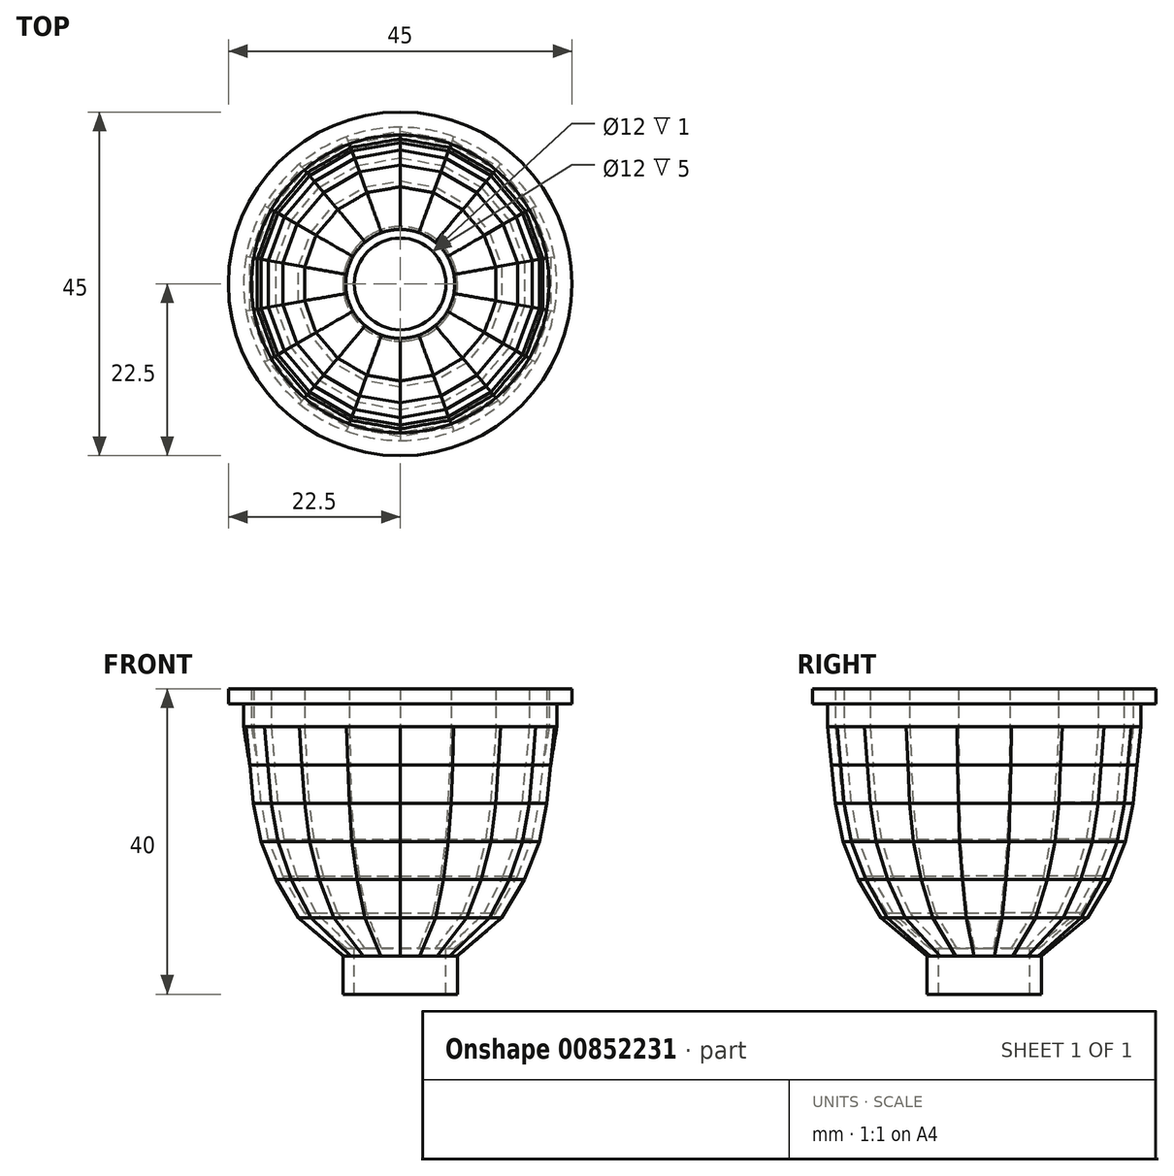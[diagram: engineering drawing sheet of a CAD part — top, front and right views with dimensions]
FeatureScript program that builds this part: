
annotation { "Feature Type Name" : "Feature", "Feature Type Description" : "" }
export const myFeature = defineFeature(function(context is Context, id is Id, definition is map)
    precondition{}
    {
        {
            var Q0;
            Q0=qCreatedBy(makeId("Top.planeOp"),FACE);
            var sketch = newSketch(context, id + "F0", { "sketchPlane" : qUnion([Q0])});
            skCircle(sketch, "E0", {"center": v(0, 0) * mm, "radius": 7.5 * mm});
            skSolve(sketch);
        }
        {
            var Q0;
            Q0=makeQuery(id+"F0.imprint","IMPRINT",FACE,{"disambiguationData":[TD([[makeQuery(id+"F0.imprint","IMPRINT",EDGE,{"derivedFrom":sQuery(id+"F0.wireOp",EDGE,"E0")}),1.0]])]});
            extrude(context, id + "F1", {"entities" : qUnion([Q0]), "depth" : 5 * mm, "offsetDistance" : 25 * mm});
        }
        {
            var Q0;
            Q0=makeQuery(id+"F1.opExtrude","CAP_FACE",FACE,{"disambiguationData":[OSD([sQuery(id+"F0.wireOp",EDGE,"E0")])],"isStart":false});
            cPlane(context, id + "F2", {"entities" : qUnion([Q0]), "cplaneType" : CPlaneType.OFFSET, "offset" : 5 * mm, "width" : 150 * mm, "height" : 150 * mm});
        }
        {
            var Q0;
            Q0=qCreatedBy(id+"F2.planeOp",FACE);
            var sketch = newSketch(context, id + "F3", { "sketchPlane" : qUnion([Q0])});
            skCircle(sketch, "E1.cCircle", {"center": v(0, 0) * mm, "radius": 13.5 * mm, "construction": true});
            skLineSegment(sketch, "E1.0", {"start": v(13.3, 2.34) * mm, "end": v(13.3, -2.34) * mm});
            skLineSegment(sketch, "E1.1", {"start": v(13.3, -2.34) * mm, "end": v(11.7, -6.75) * mm});
            skLineSegment(sketch, "E1.2", {"start": v(11.7, -6.75) * mm, "end": v(8.68, -10.34) * mm});
            skLineSegment(sketch, "E1.3", {"start": v(8.68, -10.34) * mm, "end": v(4.62, -12.69) * mm});
            skLineSegment(sketch, "E1.4", {"start": v(4.62, -12.69) * mm, "end": v(0, -13.5) * mm});
            skLineSegment(sketch, "E1.5", {"start": v(0, -13.5) * mm, "end": v(-4.62, -12.69) * mm});
            skLineSegment(sketch, "E1.6", {"start": v(-4.62, -12.69) * mm, "end": v(-8.68, -10.34) * mm});
            skLineSegment(sketch, "E1.7", {"start": v(-8.68, -10.34) * mm, "end": v(-11.7, -6.75) * mm});
            skLineSegment(sketch, "E1.8", {"start": v(-11.7, -6.75) * mm, "end": v(-13.3, -2.34) * mm});
            skLineSegment(sketch, "E1.9", {"start": v(-13.3, -2.34) * mm, "end": v(-13.3, 2.34) * mm});
            skLineSegment(sketch, "E1.10", {"start": v(-13.3, 2.34) * mm, "end": v(-11.7, 6.75) * mm});
            skLineSegment(sketch, "E1.11", {"start": v(-11.7, 6.75) * mm, "end": v(-8.68, 10.34) * mm});
            skLineSegment(sketch, "E1.12", {"start": v(-8.68, 10.34) * mm, "end": v(-4.62, 12.69) * mm});
            skLineSegment(sketch, "E1.13", {"start": v(-4.62, 12.69) * mm, "end": v(0, 13.5) * mm});
            skLineSegment(sketch, "E1.14", {"start": v(0, 13.5) * mm, "end": v(4.62, 12.69) * mm});
            skLineSegment(sketch, "E1.15", {"start": v(4.62, 12.69) * mm, "end": v(8.68, 10.34) * mm});
            skLineSegment(sketch, "E1.16", {"start": v(8.68, 10.34) * mm, "end": v(11.7, 6.75) * mm});
            skLineSegment(sketch, "E1.17", {"start": v(11.7, 6.75) * mm, "end": v(13.3, 2.34) * mm});
            skLineSegment(sketch, "E2", {"start": v(-30.47, 0) * mm, "end": v(35.34, 0) * mm, "construction": true});
            skSolve(sketch);
        }
        {
            var Q0;
            Q0=makeQuery(id+"F1.opExtrude","CAP_FACE",FACE,{"disambiguationData":[OSD([sQuery(id+"F0.wireOp",EDGE,"E0")])],"isStart":false});
            var Q1;
            Q1=makeQuery(id+"F3.imprint","IMPRINT",FACE,{"disambiguationData":[TD([[makeQuery(id+"F3.imprint","IMPRINT",EDGE,{"derivedFrom":sQuery(id+"F3.wireOp",EDGE,"E1.0")}),-1.0]])]});
            loft(context, id + "F4", {"sheetProfilesArray" : [{ "sheetProfileEntities" : qUnion([Q0]) }, { "sheetProfileEntities" : qUnion([Q1]) }]});
        }
        {
            var Q0;
            Q0=makeQuery(id+"F4.opLoft","CAP_FACE",FACE,{"disambiguationData":[OSD([makeQuery(id+"F3.imprint","IMPRINT",FACE,{"disambiguationData":[TD([[makeQuery(id+"F3.imprint","IMPRINT",EDGE,{"derivedFrom":sQuery(id+"F3.wireOp",EDGE,"E1.0")}),-1.0]])]})])],"isStart":true});
            cPlane(context, id + "F5", {"entities" : qUnion([Q0]), "cplaneType" : CPlaneType.OFFSET, "offset" : 5 * mm, "width" : 150 * mm, "height" : 150 * mm});
        }
        {
            var Q0;
            Q0=qCreatedBy(id+"F5.planeOp",FACE);
            var sketch = newSketch(context, id + "F6", { "sketchPlane" : qUnion([Q0])});
            skCircle(sketch, "E3.cCircle", {"center": v(0, 0) * mm, "radius": 16.5 * mm, "construction": true});
            skLineSegment(sketch, "E3.0", {"start": v(14.29, 8.25) * mm, "end": v(16.25, 2.87) * mm});
            skLineSegment(sketch, "E3.1", {"start": v(16.25, 2.87) * mm, "end": v(16.25, -2.87) * mm});
            skLineSegment(sketch, "E3.2", {"start": v(16.25, -2.87) * mm, "end": v(14.29, -8.25) * mm});
            skLineSegment(sketch, "E3.3", {"start": v(14.29, -8.25) * mm, "end": v(10.6, -12.64) * mm});
            skLineSegment(sketch, "E3.4", {"start": v(10.6, -12.64) * mm, "end": v(5.64, -15.5) * mm});
            skLineSegment(sketch, "E3.5", {"start": v(5.64, -15.5) * mm, "end": v(0, -16.5) * mm});
            skLineSegment(sketch, "E3.6", {"start": v(0, -16.5) * mm, "end": v(-5.64, -15.5) * mm});
            skLineSegment(sketch, "E3.7", {"start": v(-5.64, -15.5) * mm, "end": v(-10.6, -12.64) * mm});
            skLineSegment(sketch, "E3.8", {"start": v(-10.6, -12.64) * mm, "end": v(-14.29, -8.25) * mm});
            skLineSegment(sketch, "E3.9", {"start": v(-14.29, -8.25) * mm, "end": v(-16.25, -2.87) * mm});
            skLineSegment(sketch, "E3.10", {"start": v(-16.25, -2.87) * mm, "end": v(-16.25, 2.87) * mm});
            skLineSegment(sketch, "E3.11", {"start": v(-16.25, 2.87) * mm, "end": v(-14.29, 8.25) * mm});
            skLineSegment(sketch, "E3.12", {"start": v(-14.29, 8.25) * mm, "end": v(-10.6, 12.64) * mm});
            skLineSegment(sketch, "E3.13", {"start": v(-10.6, 12.64) * mm, "end": v(-5.64, 15.5) * mm});
            skLineSegment(sketch, "E3.14", {"start": v(-5.64, 15.5) * mm, "end": v(0, 16.5) * mm});
            skLineSegment(sketch, "E3.15", {"start": v(0, 16.5) * mm, "end": v(5.64, 15.5) * mm});
            skLineSegment(sketch, "E3.16", {"start": v(5.64, 15.5) * mm, "end": v(10.6, 12.64) * mm});
            skLineSegment(sketch, "E3.17", {"start": v(10.6, 12.64) * mm, "end": v(14.29, 8.25) * mm});
            skSolve(sketch);
        }
        {
            var Q1;
            Q1=makeQuery(id+"F4.opLoft","CAP_FACE",FACE,{"disambiguationData":[OSD([makeQuery(id+"F3.imprint","IMPRINT",FACE,{"disambiguationData":[TD([[makeQuery(id+"F3.imprint","IMPRINT",EDGE,{"derivedFrom":sQuery(id+"F3.wireOp",EDGE,"E1.0")}),-1.0]])]})])],"isStart":true});
            var Q2;
            Q2=makeQuery(id+"F6.imprint","IMPRINT",FACE,{"disambiguationData":[TD([[makeQuery(id+"F6.imprint","IMPRINT",EDGE,{"derivedFrom":sQuery(id+"F6.wireOp",EDGE,"E3.0")}),-1.0]])]});
            loft(context, id + "F7", {"operationType" : NewBodyOperationType.ADD, "sheetProfilesArray" : [{ "sheetProfileEntities" : qUnion([Q1]) }, { "sheetProfileEntities" : qUnion([Q2]) }]});
        }
        {
            var Q0;
            Q0=makeQuery(id+"F7.opLoft","CAP_FACE",FACE,{"disambiguationData":[OSD([makeQuery(id+"F6.imprint","IMPRINT",FACE,{"disambiguationData":[TD([[makeQuery(id+"F6.imprint","IMPRINT",EDGE,{"derivedFrom":sQuery(id+"F6.wireOp",EDGE,"E3.0")}),-1.0]])]})])],"isStart":true});
            cPlane(context, id + "F8", {"entities" : qUnion([Q0]), "cplaneType" : CPlaneType.OFFSET, "offset" : 5 * mm, "width" : 150 * mm, "height" : 150 * mm});
        }
        {
            var Q0;
            Q0=qCreatedBy(id+"F8.planeOp",FACE);
            var sketch = newSketch(context, id + "F9", { "sketchPlane" : qUnion([Q0])});
            skCircle(sketch, "E4.cCircle", {"center": v(0, 0) * mm, "radius": 18.5 * mm, "construction": true});
            skLineSegment(sketch, "E4.0", {"start": v(16.02, 9.25) * mm, "end": v(18.22, 3.21) * mm});
            skLineSegment(sketch, "E4.1", {"start": v(18.22, 3.21) * mm, "end": v(18.22, -3.21) * mm});
            skLineSegment(sketch, "E4.2", {"start": v(18.22, -3.21) * mm, "end": v(16.02, -9.25) * mm});
            skLineSegment(sketch, "E4.3", {"start": v(16.02, -9.25) * mm, "end": v(11.9, -14.17) * mm});
            skLineSegment(sketch, "E4.4", {"start": v(11.9, -14.17) * mm, "end": v(6.33, -17.38) * mm});
            skLineSegment(sketch, "E4.5", {"start": v(6.33, -17.38) * mm, "end": v(0, -18.5) * mm});
            skLineSegment(sketch, "E4.6", {"start": v(0, -18.5) * mm, "end": v(-6.33, -17.38) * mm});
            skLineSegment(sketch, "E4.7", {"start": v(-6.33, -17.38) * mm, "end": v(-11.9, -14.17) * mm});
            skLineSegment(sketch, "E4.8", {"start": v(-11.9, -14.17) * mm, "end": v(-16.02, -9.25) * mm});
            skLineSegment(sketch, "E4.9", {"start": v(-16.02, -9.25) * mm, "end": v(-18.22, -3.21) * mm});
            skLineSegment(sketch, "E4.10", {"start": v(-18.22, -3.21) * mm, "end": v(-18.22, 3.21) * mm});
            skLineSegment(sketch, "E4.11", {"start": v(-18.22, 3.21) * mm, "end": v(-16.02, 9.25) * mm});
            skLineSegment(sketch, "E4.12", {"start": v(-16.02, 9.25) * mm, "end": v(-11.9, 14.17) * mm});
            skLineSegment(sketch, "E4.13", {"start": v(-11.9, 14.17) * mm, "end": v(-6.33, 17.38) * mm});
            skLineSegment(sketch, "E4.14", {"start": v(-6.33, 17.38) * mm, "end": v(0, 18.5) * mm});
            skLineSegment(sketch, "E4.15", {"start": v(0, 18.5) * mm, "end": v(6.33, 17.38) * mm});
            skLineSegment(sketch, "E4.16", {"start": v(6.33, 17.38) * mm, "end": v(11.9, 14.17) * mm});
            skLineSegment(sketch, "E4.17", {"start": v(11.9, 14.17) * mm, "end": v(16.02, 9.25) * mm});
            skSolve(sketch);
        }
        {
            var Q1;
            Q1=makeQuery(id+"F7.opLoft","CAP_FACE",FACE,{"disambiguationData":[OSD([makeQuery(id+"F6.imprint","IMPRINT",FACE,{"disambiguationData":[TD([[makeQuery(id+"F6.imprint","IMPRINT",EDGE,{"derivedFrom":sQuery(id+"F6.wireOp",EDGE,"E3.0")}),-1.0]])]})])],"isStart":true});
            var Q2;
            Q2=makeQuery(id+"F9.imprint","IMPRINT",FACE,{"disambiguationData":[TD([[makeQuery(id+"F9.imprint","IMPRINT",EDGE,{"derivedFrom":sQuery(id+"F9.wireOp",EDGE,"E4.0")}),-1.0]])]});
            loft(context, id + "F10", {"operationType" : NewBodyOperationType.ADD, "sheetProfilesArray" : [{ "sheetProfileEntities" : qUnion([Q1]) }, { "sheetProfileEntities" : qUnion([Q2]) }]});
        }
        {
            var Q0;
            Q0=makeQuery(id+"F10.opLoft","CAP_FACE",FACE,{"disambiguationData":[OSD([makeQuery(id+"F9.imprint","IMPRINT",FACE,{"disambiguationData":[TD([[makeQuery(id+"F9.imprint","IMPRINT",EDGE,{"derivedFrom":sQuery(id+"F9.wireOp",EDGE,"E4.0")}),-1.0]])]})])],"isStart":true});
            cPlane(context, id + "F11", {"entities" : qUnion([Q0]), "cplaneType" : CPlaneType.OFFSET, "offset" : 5 * mm, "width" : 150 * mm, "height" : 150 * mm});
        }
        {
            var Q0;
            Q0=qCreatedBy(id+"F11.planeOp",FACE);
            var sketch = newSketch(context, id + "F12", { "sketchPlane" : qUnion([Q0])});
            skCircle(sketch, "E5.cCircle", {"center": v(0, 0) * mm, "radius": 19.5 * mm, "construction": true});
            skLineSegment(sketch, "E5.0", {"start": v(16.89, 9.75) * mm, "end": v(19.2, 3.39) * mm});
            skLineSegment(sketch, "E5.1", {"start": v(19.2, 3.39) * mm, "end": v(19.2, -3.39) * mm});
            skLineSegment(sketch, "E5.2", {"start": v(19.2, -3.39) * mm, "end": v(16.89, -9.75) * mm});
            skLineSegment(sketch, "E5.3", {"start": v(16.89, -9.75) * mm, "end": v(12.53, -14.94) * mm});
            skLineSegment(sketch, "E5.4", {"start": v(12.53, -14.94) * mm, "end": v(6.67, -18.32) * mm});
            skLineSegment(sketch, "E5.5", {"start": v(6.67, -18.32) * mm, "end": v(0, -19.5) * mm});
            skLineSegment(sketch, "E5.6", {"start": v(0, -19.5) * mm, "end": v(-6.67, -18.32) * mm});
            skLineSegment(sketch, "E5.7", {"start": v(-6.67, -18.32) * mm, "end": v(-12.53, -14.94) * mm});
            skLineSegment(sketch, "E5.8", {"start": v(-12.53, -14.94) * mm, "end": v(-16.89, -9.75) * mm});
            skLineSegment(sketch, "E5.9", {"start": v(-16.89, -9.75) * mm, "end": v(-19.2, -3.39) * mm});
            skLineSegment(sketch, "E5.10", {"start": v(-19.2, -3.39) * mm, "end": v(-19.2, 3.39) * mm});
            skLineSegment(sketch, "E5.11", {"start": v(-19.2, 3.39) * mm, "end": v(-16.89, 9.75) * mm});
            skLineSegment(sketch, "E5.12", {"start": v(-16.89, 9.75) * mm, "end": v(-12.53, 14.94) * mm});
            skLineSegment(sketch, "E5.13", {"start": v(-12.53, 14.94) * mm, "end": v(-6.67, 18.32) * mm});
            skLineSegment(sketch, "E5.14", {"start": v(-6.67, 18.32) * mm, "end": v(0, 19.5) * mm});
            skLineSegment(sketch, "E5.15", {"start": v(0, 19.5) * mm, "end": v(6.67, 18.32) * mm});
            skLineSegment(sketch, "E5.16", {"start": v(6.67, 18.32) * mm, "end": v(12.53, 14.94) * mm});
            skLineSegment(sketch, "E5.17", {"start": v(12.53, 14.94) * mm, "end": v(16.89, 9.75) * mm});
            skSolve(sketch);
        }
        {
            var Q1;
            Q1=makeQuery(id+"F10.opLoft","CAP_FACE",FACE,{"disambiguationData":[OSD([makeQuery(id+"F9.imprint","IMPRINT",FACE,{"disambiguationData":[TD([[makeQuery(id+"F9.imprint","IMPRINT",EDGE,{"derivedFrom":sQuery(id+"F9.wireOp",EDGE,"E4.0")}),-1.0]])]})])],"isStart":true});
            var Q2;
            Q2=makeQuery(id+"F12.imprint","IMPRINT",FACE,{"disambiguationData":[TD([[makeQuery(id+"F12.imprint","IMPRINT",EDGE,{"derivedFrom":sQuery(id+"F12.wireOp",EDGE,"E5.0")}),-1.0]])]});
            loft(context, id + "F13", {"operationType" : NewBodyOperationType.ADD, "sheetProfilesArray" : [{ "sheetProfileEntities" : qUnion([Q1]) }, { "sheetProfileEntities" : qUnion([Q2]) }]});
        }
        {
            var Q0;
            Q0=makeQuery(id+"F13.opLoft","CAP_FACE",FACE,{"disambiguationData":[OSD([makeQuery(id+"F12.imprint","IMPRINT",FACE,{"disambiguationData":[TD([[makeQuery(id+"F12.imprint","IMPRINT",EDGE,{"derivedFrom":sQuery(id+"F12.wireOp",EDGE,"E5.0")}),-1.0]])]})])],"isStart":true});
            cPlane(context, id + "F14", {"entities" : qUnion([Q0]), "cplaneType" : CPlaneType.OFFSET, "offset" : 5 * mm, "width" : 150 * mm, "height" : 150 * mm});
        }
        {
            var Q0;
            Q0=qCreatedBy(id+"F14.planeOp",FACE);
            var sketch = newSketch(context, id + "F15", { "sketchPlane" : qUnion([Q0])});
            skCircle(sketch, "E6.cCircle", {"center": v(0, 0) * mm, "radius": 20 * mm, "construction": true});
            skLineSegment(sketch, "E6.0", {"start": v(19.7, 3.47) * mm, "end": v(19.7, -3.47) * mm});
            skLineSegment(sketch, "E6.1", {"start": v(19.7, -3.47) * mm, "end": v(17.32, -10) * mm});
            skLineSegment(sketch, "E6.2", {"start": v(17.32, -10) * mm, "end": v(12.86, -15.32) * mm});
            skLineSegment(sketch, "E6.3", {"start": v(12.86, -15.32) * mm, "end": v(6.84, -18.8) * mm});
            skLineSegment(sketch, "E6.4", {"start": v(6.84, -18.8) * mm, "end": v(0, -20) * mm});
            skLineSegment(sketch, "E6.5", {"start": v(0, -20) * mm, "end": v(-6.84, -18.8) * mm});
            skLineSegment(sketch, "E6.6", {"start": v(-6.84, -18.8) * mm, "end": v(-12.86, -15.32) * mm});
            skLineSegment(sketch, "E6.7", {"start": v(-12.86, -15.32) * mm, "end": v(-17.32, -10) * mm});
            skLineSegment(sketch, "E6.8", {"start": v(-17.32, -10) * mm, "end": v(-19.7, -3.47) * mm});
            skLineSegment(sketch, "E6.9", {"start": v(-19.7, -3.47) * mm, "end": v(-19.7, 3.47) * mm});
            skLineSegment(sketch, "E6.10", {"start": v(-19.7, 3.47) * mm, "end": v(-17.32, 10) * mm});
            skLineSegment(sketch, "E6.11", {"start": v(-17.32, 10) * mm, "end": v(-12.86, 15.32) * mm});
            skLineSegment(sketch, "E6.12", {"start": v(-12.86, 15.32) * mm, "end": v(-6.84, 18.8) * mm});
            skLineSegment(sketch, "E6.13", {"start": v(-6.84, 18.8) * mm, "end": v(0, 20) * mm});
            skLineSegment(sketch, "E6.14", {"start": v(0, 20) * mm, "end": v(6.84, 18.8) * mm});
            skLineSegment(sketch, "E6.15", {"start": v(6.84, 18.8) * mm, "end": v(12.86, 15.32) * mm});
            skLineSegment(sketch, "E6.16", {"start": v(12.86, 15.32) * mm, "end": v(17.32, 10) * mm});
            skLineSegment(sketch, "E6.17", {"start": v(17.32, 10) * mm, "end": v(19.7, 3.47) * mm});
            skSolve(sketch);
        }
        {
            var Q1;
            Q1=makeQuery(id+"F13.opLoft","CAP_FACE",FACE,{"disambiguationData":[OSD([makeQuery(id+"F12.imprint","IMPRINT",FACE,{"disambiguationData":[TD([[makeQuery(id+"F12.imprint","IMPRINT",EDGE,{"derivedFrom":sQuery(id+"F12.wireOp",EDGE,"E5.0")}),-1.0]])]})])],"isStart":true});
            var Q2;
            Q2=makeQuery(id+"F15.imprint","IMPRINT",FACE,{"disambiguationData":[TD([[makeQuery(id+"F15.imprint","IMPRINT",EDGE,{"derivedFrom":sQuery(id+"F15.wireOp",EDGE,"E6.0")}),-1.0]])]});
            loft(context, id + "F16", {"operationType" : NewBodyOperationType.ADD, "sheetProfilesArray" : [{ "sheetProfileEntities" : qUnion([Q1]) }, { "sheetProfileEntities" : qUnion([Q2]) }]});
        }
        {
            var Q0;
            Q0=makeQuery(id+"F16.opLoft","CAP_FACE",FACE,{"disambiguationData":[OSD([makeQuery(id+"F15.imprint","IMPRINT",FACE,{"disambiguationData":[TD([[makeQuery(id+"F15.imprint","IMPRINT",EDGE,{"derivedFrom":sQuery(id+"F15.wireOp",EDGE,"E6.0")}),-1.0]])]})])],"isStart":true});
            cPlane(context, id + "F17", {"entities" : qUnion([Q0]), "cplaneType" : CPlaneType.OFFSET, "offset" : 5 * mm, "width" : 150 * mm, "height" : 150 * mm});
        }
        {
            var Q0;
            Q0=qCreatedBy(id+"F17.planeOp",FACE);
            var sketch = newSketch(context, id + "F18", { "sketchPlane" : qUnion([Q0])});
            skCircle(sketch, "E7", {"center": v(0, 0) * mm, "radius": 20.5 * mm});
            skSolve(sketch);
        }
        {
            var Q1;
            Q1=makeQuery(id+"F16.opLoft","CAP_FACE",FACE,{"disambiguationData":[OSD([makeQuery(id+"F15.imprint","IMPRINT",FACE,{"disambiguationData":[TD([[makeQuery(id+"F15.imprint","IMPRINT",EDGE,{"derivedFrom":sQuery(id+"F15.wireOp",EDGE,"E6.0")}),-1.0]])]})])],"isStart":true});
            var Q2;
            Q2=makeQuery(id+"F18.imprint","IMPRINT",FACE,{"disambiguationData":[TD([[makeQuery(id+"F18.imprint","IMPRINT",EDGE,{"derivedFrom":sQuery(id+"F18.wireOp",EDGE,"E7")}),1.0]])]});
            loft(context, id + "F19", {"operationType" : NewBodyOperationType.ADD, "sheetProfilesArray" : [{ "sheetProfileEntities" : qUnion([Q1]) }, { "sheetProfileEntities" : qUnion([Q2]) }]});
        }
        {
            var Q0;
            Q0=makeQuery(id+"F19.opLoft","CAP_FACE",FACE,{"disambiguationData":[OSD([makeQuery(id+"F18.imprint","IMPRINT",FACE,{"disambiguationData":[TD([[makeQuery(id+"F18.imprint","IMPRINT",EDGE,{"derivedFrom":sQuery(id+"F18.wireOp",EDGE,"E7")}),1.0]])]})])],"isStart":true});
            shell(context, id + "F20", {"entities" : qUnion([Q0]), "thickness" : 1 * mm});
        }
        {
            var Q0;
            {var subQ0=sQuery(id+"F0.wireOp",EDGE,"E0");Q0=makeQuery(id+"F20.opShell","OFFSET_FACE",FACE,{"disambiguationData":[OSD([subQ0]),TDD([makeQuery(id+"F1.opExtrude","CAP_FACE",FACE,{"disambiguationData":[OSD([subQ0])],"isStart":true})])]});}
            var sketch = newSketch(context, id + "F21", { "sketchPlane" : qUnion([Q0])});
            skCircle(sketch, "E8", {"center": v(0, 0) * mm, "radius": 6 * mm});
            skSolve(sketch);
        }
        {
            var Q0;
            Q0=makeQuery(id+"F21.imprint","IMPRINT",FACE,{"disambiguationData":[TD([[makeQuery(id+"F21.imprint","IMPRINT",EDGE,{"derivedFrom":sQuery(id+"F21.wireOp",EDGE,"E8")}),1.0]])]});
            extrude(context, id + "F22", {"entities" : qUnion([Q0]), "operationType" : NewBodyOperationType.REMOVE, "endBound" : BoundingType.THROUGH_ALL, "oppositeDirection" : true, "depth" : 25 * mm, "offsetDistance" : 25 * mm});
        }
        {
            var Q0;
            Q0=makeQuery(id+"F19.opLoft","CAP_FACE",FACE,{"disambiguationData":[OSD([makeQuery(id+"F18.imprint","IMPRINT",FACE,{"disambiguationData":[TD([[makeQuery(id+"F18.imprint","IMPRINT",EDGE,{"derivedFrom":sQuery(id+"F18.wireOp",EDGE,"E7")}),1.0]])]})])],"isStart":true});
            extrude(context, id + "F23", {"entities" : qUnion([Q0]), "operationType" : NewBodyOperationType.ADD, "depth" : 5 * mm, "offsetDistance" : 25 * mm});
        }
        {
            var Q0;
            Q0=qCreatedBy(makeId("Front.planeOp"),FACE);
            var sketch = newSketch(context, id + "F24", { "sketchPlane" : qUnion([Q0])});
            skLineSegment(sketch, "E9", {"start": v(-20.5, 40) * mm, "end": v(-22.5, 40) * mm});
            skLineSegment(sketch, "E10", {"start": v(-22.5, 40) * mm, "end": v(-22.5, 38) * mm});
            skLineSegment(sketch, "E11", {"start": v(-20.5, 40) * mm, "end": v(-20.5, 38) * mm});
            skLineSegment(sketch, "E12", {"start": v(-22.5, 38) * mm, "end": v(-20.5, 38) * mm});
            skLineSegment(sketch, "E13", {"start": v(0, 0) * mm, "end": v(0, 111.4) * mm, "construction": true});
            skSolve(sketch);
        }
        {
            var Q0;
            Q0 = qSketchRegion(id + "F24", true);
            var Q1;
            Q1=sQuery(id+"F24.wireOp",EDGE,"E13");
            revolve(context, id + "F25", {"operationType" : NewBodyOperationType.ADD, "surfaceOperationType" : NewSurfaceOperationType.NEW, "entities" : qUnion([Q0]), "axis" : qUnion([Q1]), "revolveType" : RevolveType.FULL});
        }
    });
